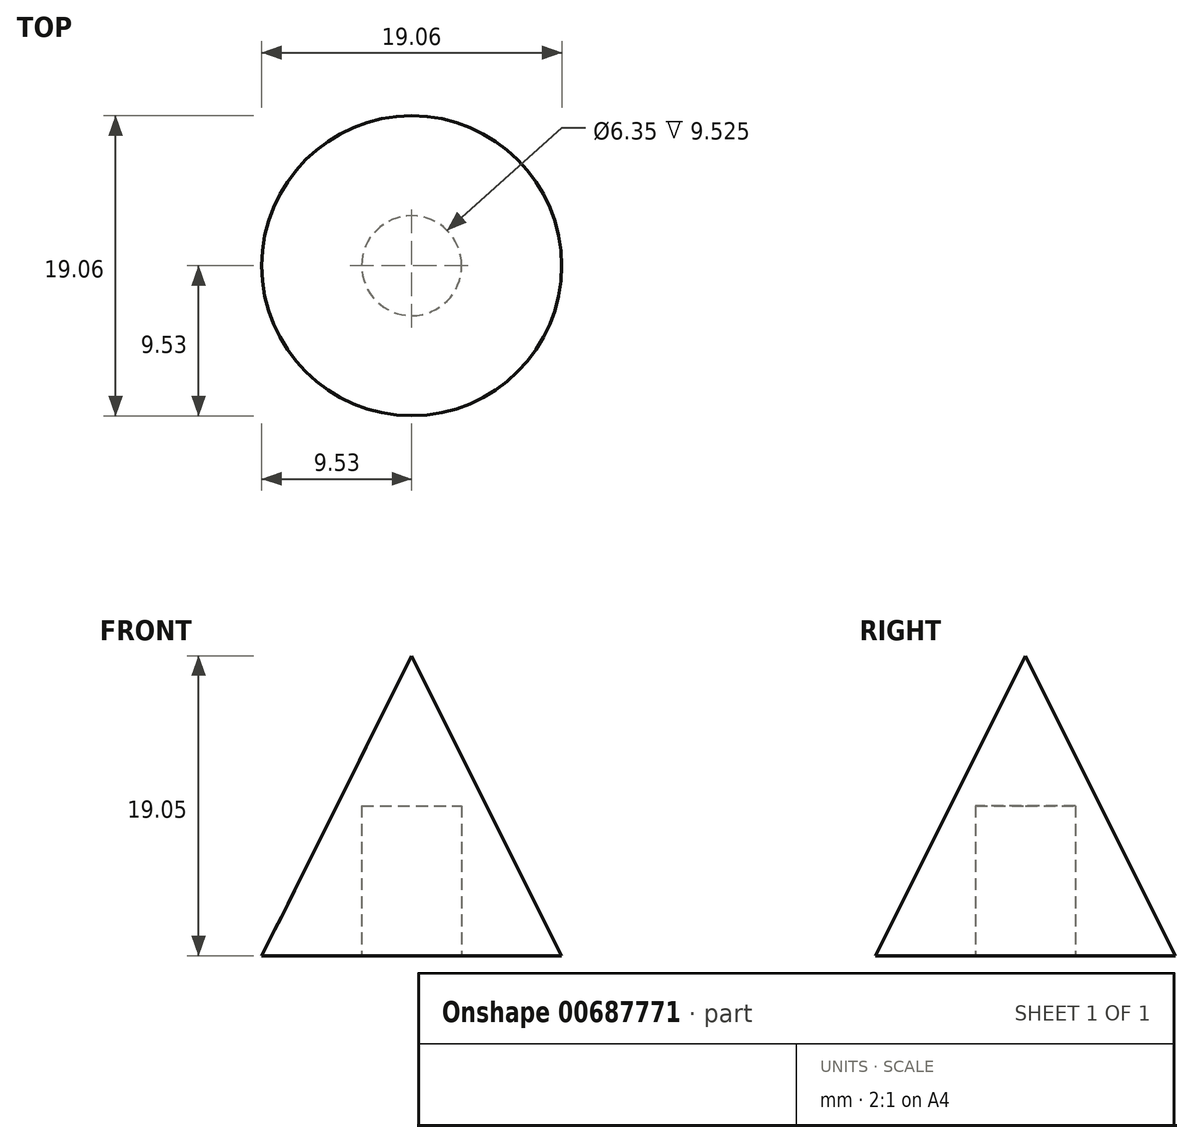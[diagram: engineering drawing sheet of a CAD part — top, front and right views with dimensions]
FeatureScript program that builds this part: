
annotation { "Feature Type Name" : "Feature", "Feature Type Description" : "" }
export const myFeature = defineFeature(function(context is Context, id is Id, definition is map)
    precondition{}
    {
        {
            var Q0;
            Q0=qCreatedBy(makeId("Front.planeOp"),FACE);
            var sketch = newSketch(context, id + "F0", { "sketchPlane" : qUnion([Q0])});
            skLineSegment(sketch, "E0", {"start": v(0, 0) * mm, "end": v(0, 19.05) * mm});
            skLineSegment(sketch, "E1", {"start": v(0, 0) * mm, "end": v(9.53, 0) * mm});
            skLineSegment(sketch, "E2", {"start": v(9.53, 0) * mm, "end": v(0, 19.05) * mm});
            skSolve(sketch);
        }
        {
            var Q0;
            Q0=makeQuery(id+"F0.imprint","IMPRINT",FACE,{"disambiguationData":[TD([[makeQuery(id+"F0.imprint","IMPRINT",EDGE,{"derivedFrom":sQuery(id+"F0.wireOp",EDGE,"E0")}),-1.0]])]});
            var Q1;
            Q1=sQuery(id+"F0.wireOp",EDGE,"E0");
            revolve(context, id + "F1", {"entities" : qUnion([Q0]), "axis" : qUnion([Q1]), "revolveType" : RevolveType.FULL});
        }
        {
            var Q0;
            Q0=makeQuery(id+"F1.opRevolve","SWEPT_FACE",FACE,{"disambiguationData":[OSD([sQuery(id+"F0.wireOp",EDGE,"E1")])]});
            var sketch = newSketch(context, id + "F2", { "sketchPlane" : qUnion([Q0])});
            skCircle(sketch, "E3", {"center": v(0, 0) * mm, "radius": 3.18 * mm});
            skSolve(sketch);
        }
        {
            var Q0;
            Q0 = qSketchRegion(id + "F2", true);
            extrude(context, id + "F3", {"entities" : qUnion([Q0]), "operationType" : NewBodyOperationType.REMOVE, "oppositeDirection" : true, "depth" : 9.52 * mm, "offsetDistance" : 25.4 * mm});
        }
    });
